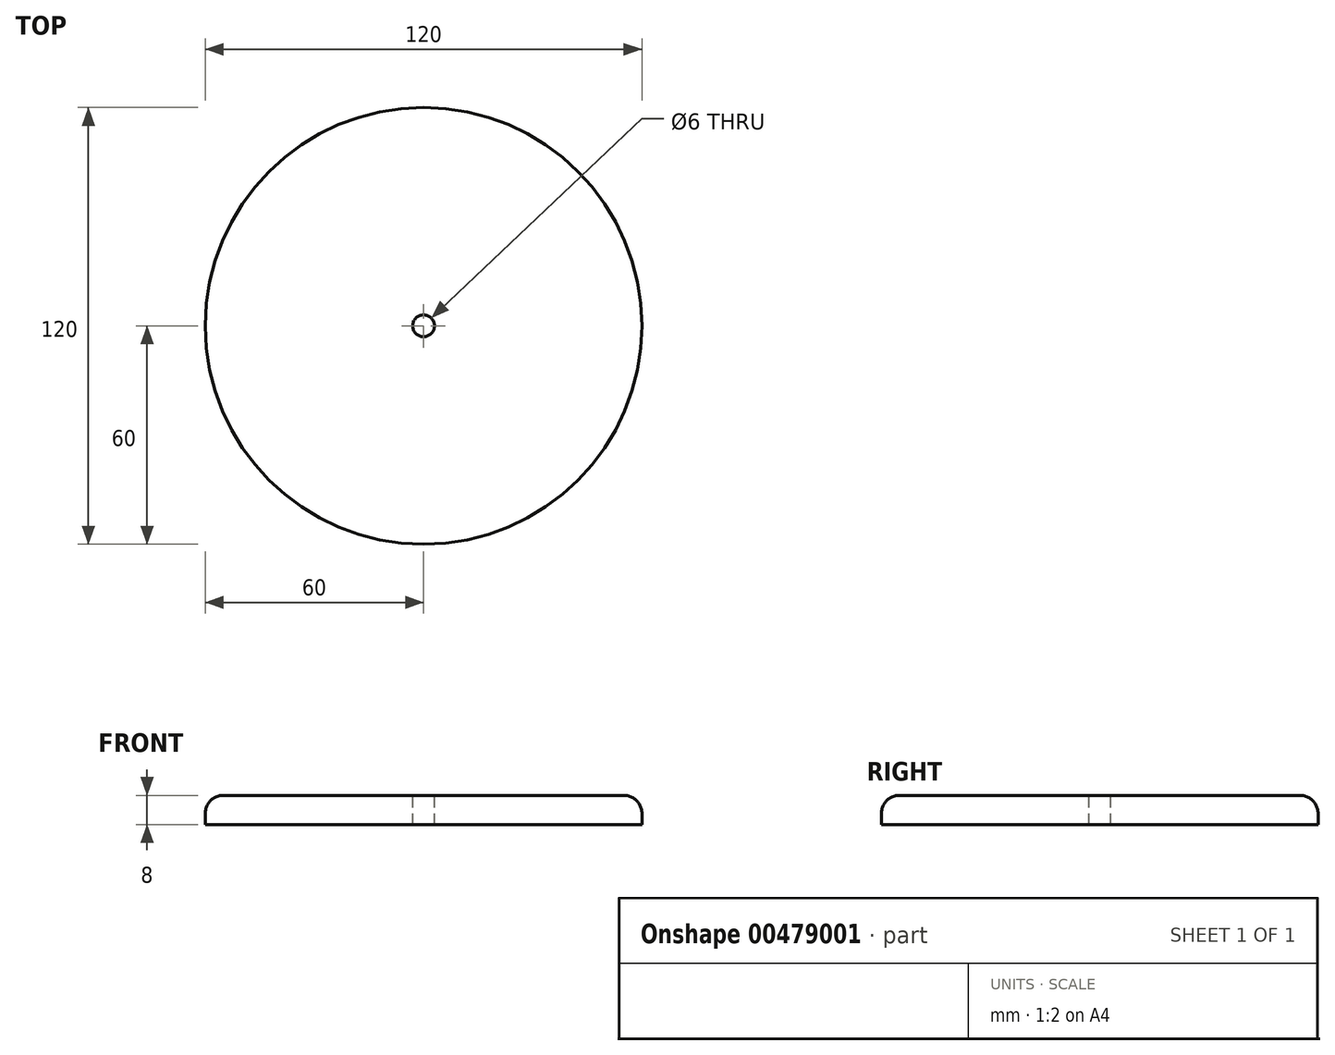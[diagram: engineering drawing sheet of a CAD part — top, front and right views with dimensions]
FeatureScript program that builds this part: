
annotation { "Feature Type Name" : "Feature", "Feature Type Description" : "" }
export const myFeature = defineFeature(function(context is Context, id is Id, definition is map)
    precondition{}
    {
        {
            var Q0;
            Q0=qCreatedBy(makeId("Front.planeOp"),FACE);
            var sketch = newSketch(context, id + "F0", { "sketchPlane" : qUnion([Q0])});
            skLineSegment(sketch, "E0.bottom", {"start": v(55, 8) * mm, "end": v(0, 8) * mm});
            skLineSegment(sketch, "E0.top", {"start": v(60, 0) * mm, "end": v(0, 0) * mm});
            skLineSegment(sketch, "E0.left", {"start": v(60, 3) * mm, "end": v(60, 0) * mm});
            skLineSegment(sketch, "E0.right", {"start": v(0, 8) * mm, "end": v(0, 0) * mm});
            skPoint(sketch, "E1.visualSharp", {"position": v(60, 8) * mm});
            skArc(sketch, "E1.filletArc", {"start": v(60, 3) * mm, "mid": v(58.54, 6.54) * mm, "end": v(55, 8) * mm});
            skSolve(sketch);
        }
        {
            var Q0;
            Q0=makeQuery(id+"F0.imprint","IMPRINT",FACE,{"disambiguationData":[TD([[makeQuery(id+"F0.imprint","IMPRINT",EDGE,{"derivedFrom":sQuery(id+"F0.wireOp",EDGE,"E0.bottom")}),1.0]])]});
            var Q1;
            Q1=sQuery(id+"F0.wireOp",EDGE,"E0.right");
            revolve(context, id + "F1", {"entities" : qUnion([Q0]), "axis" : qUnion([Q1]), "revolveType" : RevolveType.FULL});
        }
        {
            var Q0;
            Q0=makeQuery(id+"F1.opRevolve","SWEPT_FACE",FACE,{"disambiguationData":[OSD([sQuery(id+"F0.wireOp",EDGE,"E0.bottom")])]});
            var sketch = newSketch(context, id + "F2", { "sketchPlane" : qUnion([Q0])});
            skCircle(sketch, "E2", {"center": v(0, 0) * mm, "radius": 3 * mm});
            skSolve(sketch);
        }
        {
            var Q0;
            Q0=makeQuery(id+"F2.imprint","IMPRINT",FACE,{"disambiguationData":[TD([[makeQuery(id+"F2.imprint","IMPRINT",EDGE,{"derivedFrom":sQuery(id+"F2.wireOp",EDGE,"E2")}),1.0]])]});
            extrude(context, id + "F3", {"entities" : qUnion([Q0]), "operationType" : NewBodyOperationType.REMOVE, "oppositeDirection" : true, "depth" : 25 * mm});
        }
    });
